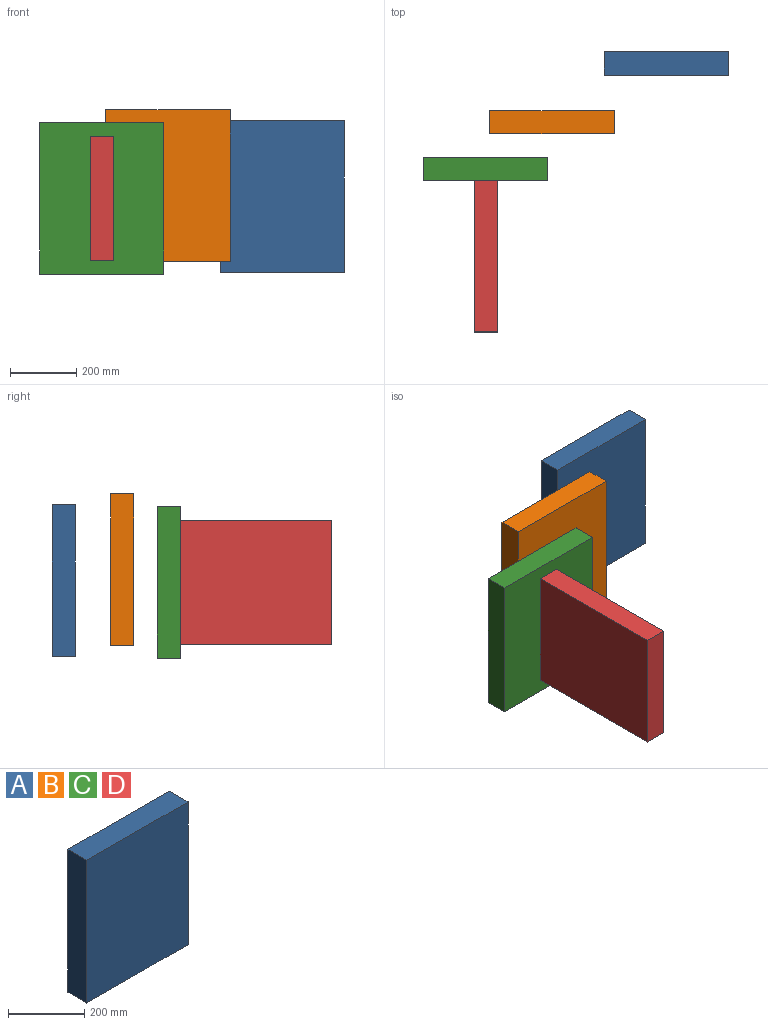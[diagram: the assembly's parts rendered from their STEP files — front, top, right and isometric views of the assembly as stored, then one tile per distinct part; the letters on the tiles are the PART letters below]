
ASSEMBLY  parts=4 mates=1
PART A: 6 faces, bbox 374.7x69.9x457.2 mm
  f0: plane 457.2x69.85mm, normal (-1,0,0), area 31935.4mm2, adj f1,f3,f4,f5
  f1: plane 374.65x69.85mm, normal (0,0,-1), area 26169.3mm2, adj f0,f2,f4,f5
  f2: plane 457.2x69.85mm, normal (1,0,0), area 31935.4mm2, adj f1,f3,f4,f5
  f3: plane 374.65x69.85mm, normal (0,0,1), area 26169.3mm2, adj f0,f2,f4,f5
  f4: plane 457.2x374.65mm, normal (0,-1,0), area 171290mm2, adj f0,f1,f2,f3
  f5: plane 457.2x374.65mm, normal (0,1,0), area 171290mm2, adj f0,f1,f2,f3
PART B: same geometry as A
PART C: same geometry as A
PART D: same geometry as A
PLACE A t=(90.55,289.41,-87.51)mm
PLACE B t=(-253.62,112.56,-54.73)mm
PLACE C t=(-453.14,-27.94,-92.69)mm
PLACE D rot(axis=(0.58,0.58,-0.58),120deg) t=(-230.89,-97.79,323.24)mm
MATE planar D.f1 <-> C.f4  axis (0,1,0) through (-265.81,-97.79,135.91)mm
